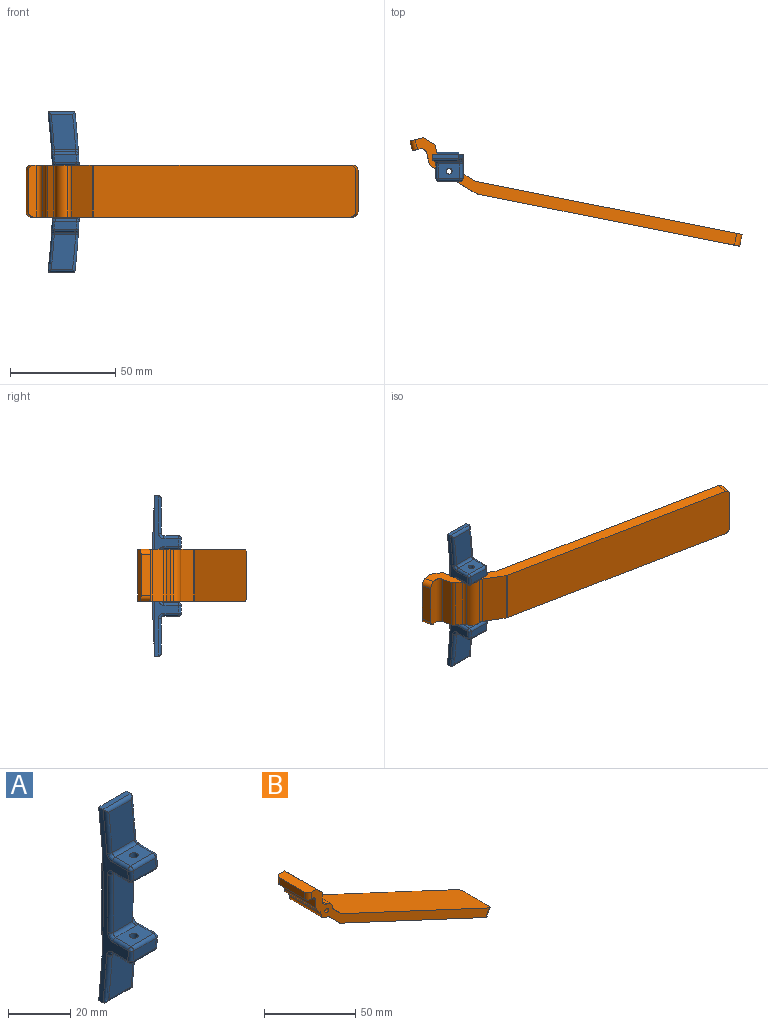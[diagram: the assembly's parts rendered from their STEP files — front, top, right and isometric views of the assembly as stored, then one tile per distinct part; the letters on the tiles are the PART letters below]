
ASSEMBLY  parts=2 mates=1
PART A: 67 faces, bbox 38x38x76.8 mm
  f0: plane 76.2x2.54mm, normal (0,1,0), area 76.9mm2, adj f4,f8,f13,f65
  f1: plane 10.16x6.99mm, normal (0,0,-1), area 64.9mm2, adj f16,f28,f29,f37,f38
  f2: cylinder r=317.5mm len=76.2mm, axis (0,1,0), area 184.2mm2, adj f6,f8,f13,f26,f27,f31,f32,f36
  f3: plane 10.16x7.63mm, normal (0,0,1), area 65.1mm2, adj f16,f45,f51,f56,f59,f60
  f4: cylinder r=317.5mm len=76.2mm, axis (0,1,0), area 230.8mm2, adj f0,f8,f13,f18,f19,f20,f23,f24
  f5: plane 10.35x3.81mm, normal (0,-1,0), area 38.7mm2, adj f38,f39,f50,f51
  f6: plane 76.2x2.29mm, normal (0,1,0), area 116.6mm2, adj f2,f66
  f7: plane 16.51x11.64mm, normal (0,-1,0), area 167.6mm2, adj f18,f21,f25,f26
  f8: plane 12.7x1.91mm, normal (0,0,1), area 24.2mm2, adj f0,f2,f4,f21,f64
  f9: plane 10.35x3.81mm, normal (0,-1,0), area 38.7mm2, adj f34,f35,f48,f49
  f10: plane 10.16x6.99mm, normal (0,0,1), area 64.9mm2, adj f15,f24,f25,f35,f36
  f11: plane 10.16x7.63mm, normal (0,0,-1), area 65.1mm2, adj f15,f40,f48,f53,f57,f58
  f12: plane 22.86x9.1mm, normal (0,-1,0), area 203.2mm2, adj f17,f46,f53,f56,f57,f60
  f13: plane 12.7x1.91mm, normal (0,0,-1), area 24.2mm2, adj f0,f2,f4,f22,f64
  f14: plane 16.51x11.64mm, normal (0,-1,0), area 167.6mm2, adj f19,f22,f27,f28
  f15: cylinder r=1.39mm len=6.35mm, axis (0,0,1), area 55.4mm2, adj f10,f11
  f16: cylinder r=1.39mm len=6.35mm, axis (0,0,1), area 55.4mm2, adj f1,f3
  f17: cone r=314.96mm half-angle=45deg, axis (0,1,0), area 69.9mm2, adj f12,f57,f60,f63
  f18: torus R=318.77mm, axis (0,-1,0), area 34.4mm2, adj f4,f7,f20,f21
  f19: torus R=318.77mm, axis (0,-1,0), area 34.4mm2, adj f4,f14,f22,f23
  f20: bspline ~3.11x2.96mm, area 5.5mm2, adj f4,f18,f24,f25
  f21: cylinder r=1.27mm len=12.7mm, axis (1,0,0), area 22.8mm2, adj f7,f8,f18,f26
  f22: cylinder r=1.27mm len=12.7mm, axis (-1,0,0), area 22.8mm2, adj f13,f14,f19,f27
  f23: bspline ~3.1x2.98mm, area 5.5mm2, adj f4,f19,f28,f29
  f24: cylinder r=1.27mm len=6.99mm, axis (0,1,0), area 14.4mm2, adj f4,f10,f20,f30
  f25: cylinder r=1.27mm len=10.31mm, axis (-1,0,0), area 20.3mm2, adj f7,f10,f20,f31
  f26: torus R=316.23mm, axis (0,-1,0), area 34.3mm2, adj f2,f7,f21,f31
  f27: torus R=316.23mm, axis (0,-1,0), area 34.3mm2, adj f2,f14,f22,f32
  f28: cylinder r=1.27mm len=10.31mm, axis (1,0,0), area 20.3mm2, adj f1,f14,f23,f32
  f29: cylinder r=1.27mm len=6.99mm, axis (0,1,0), area 14.4mm2, adj f1,f4,f23,f33
  f30: sphere r=1.27mm, area 1.7mm2, adj f24,f34,f35
  f31: bspline ~3.12x2.98mm, area 5.3mm2, adj f2,f25,f26,f36
  f32: bspline ~3.11x2.99mm, area 5.3mm2, adj f2,f27,f28,f37
  f33: sphere r=1.27mm, area 2.6mm2, adj f29,f38,f39
  f34: torus R=318.77mm, axis (0,-1,0), area 7.6mm2, adj f4,f9,f30,f41
  f35: cylinder r=1.27mm len=10.16mm, axis (1,0,0), area 20.3mm2, adj f9,f10,f30,f42
  f36: cylinder r=1.27mm len=6.99mm, axis (0,1,0), area 13.4mm2, adj f2,f10,f31,f42
  f37: cylinder r=1.27mm len=6.99mm, axis (0,1,0), area 13.4mm2, adj f1,f2,f32,f43
  f38: cylinder r=1.27mm len=10.16mm, axis (-1,0,0), area 20.3mm2, adj f1,f5,f33,f43
  f39: torus R=318.77mm, axis (0,-1,0), area 7.6mm2, adj f4,f5,f33,f44
  f40: cylinder r=1.27mm len=6.99mm, axis (0,1,0), area 13.5mm2, adj f4,f11,f41,f47
  f41: sphere r=1.27mm, area 2.5mm2, adj f34,f40,f48
  f42: sphere r=1.27mm, area 2.4mm2, adj f35,f36,f49
  f43: sphere r=1.27mm, area 3.4mm2, adj f37,f38,f50
  f44: sphere r=1.27mm, area 1.6mm2, adj f39,f45,f51
  f45: cylinder r=1.27mm len=6.99mm, axis (0,1,0), area 13.5mm2, adj f3,f4,f44,f52
  f46: torus R=318.77mm, axis (0,-1,0), area 45.5mm2, adj f4,f12,f47,f52
  f47: bspline ~3.1x2.98mm, area 5.4mm2, adj f4,f40,f46,f53
  f48: cylinder r=1.27mm len=10.16mm, axis (-1,0,0), area 20.3mm2, adj f9,f11,f41,f54
  f49: torus R=316.23mm, axis (0,-1,0), area 7.6mm2, adj f2,f9,f42,f54
  f50: torus R=316.23mm, axis (0,-1,0), area 7.6mm2, adj f2,f5,f43,f55
  f51: cylinder r=1.27mm len=10.16mm, axis (1,0,0), area 20.3mm2, adj f3,f5,f44,f55
  f52: bspline ~3.11x2.96mm, area 5.4mm2, adj f4,f45,f46,f56
  f53: cylinder r=1.27mm len=9.52mm, axis (1,0,0), area 18.4mm2, adj f11,f12,f47,f57
  f54: sphere r=1.27mm, area 3.5mm2, adj f48,f49,f58
  f55: sphere r=1.27mm, area 2.6mm2, adj f50,f51,f59
  f56: cylinder r=1.27mm len=9.52mm, axis (-1,0,0), area 18.4mm2, adj f3,f12,f52,f60
  f57: bspline ~38.03x38.01mm, area 4.6mm2, adj f11,f12,f17,f53,f61
  f58: cylinder r=1.27mm len=7.63mm, axis (0,1,0), area 15.6mm2, adj f2,f11,f54,f61
  f59: cylinder r=1.27mm len=7.63mm, axis (0,1,0), area 15.6mm2, adj f2,f3,f55,f62
  f60: bspline ~38.03x38.01mm, area 4.6mm2, adj f3,f12,f17,f56,f62
  f61: bspline ~3.93x2.92mm, area 5.9mm2, adj f2,f57,f58,f63
  f62: bspline ~3.86x3.06mm, area 5.9mm2, adj f2,f59,f60,f63
  f63: torus R=316.23mm, axis (0,-1,0), area 22.8mm2, adj f2,f17,f61,f62
  f64: cylinder r=572.13mm len=76.2mm, axis (1,0,0), area 774.8mm2, adj f8,f13,f65,f66
  f65: plane 76.2x1.27mm, normal (-1,0,0), area 64.5mm2, adj f0,f64
  f66: plane 76.2x1.27mm, normal (1,0,0), area 64.5mm2, adj f6,f64
PART B: 31 faces, bbox 142.9x24.6x85.9 mm
  f0: plane 24.64x5.48mm, normal (0.71,0,0.71), area 190.8mm2, adj f7,f19,f20,f25
  f1: plane 24.64x8.12mm, normal (-0.71,0,-0.71), area 282.9mm2, adj f3,f19,f20,f23
  f2: plane 24.64x2.38mm, normal (-0.71,0,-0.71), area 82.9mm2, adj f18,f19,f20,f24
  f3: cylinder r=2.54mm len=24.64mm, axis (0,1,0), area 21.8mm2, adj f1,f4,f19,f20
  f4: plane 115.1x53.67mm, normal (-0.42,0,-0.91), area 3126.3mm2, adj f3,f5,f19,f20,f28,f30
  f5: plane 19.56x5.22mm, normal (0.91,0,-0.42), area 112.5mm2, adj f4,f6,f28,f30
  f6: plane 116.81x54.47mm, normal (0.42,0,0.91), area 3172.7mm2, adj f5,f7,f19,f20,f28,f30
  f7: cylinder r=2.54mm len=24.64mm, axis (0,1,0), area 21.8mm2, adj f0,f6,f19,f20
  f8: plane 24.64x0.99mm, normal (0.71,0,0.71), area 34.3mm2, adj f9,f19,f20,f26
  f9: cylinder r=2.54mm len=24.64mm, axis (0,1,0), area 49.2mm2, adj f8,f10,f19,f20
  f10: plane 24.64x5.93mm, normal (1,0,0), area 146.2mm2, adj f9,f11,f19,f20
  f11: plane 24.64x4.49mm, normal (0.71,0,0.71), area 156.5mm2, adj f10,f12,f19,f20
  f12: plane 24.64x6.62mm, normal (0,0,1), area 160.4mm2, adj f11,f13,f19,f20,f27,f29
  f13: plane 19.56x4.78mm, normal (-1,0,0), area 93.4mm2, adj f12,f14,f27,f29
  f14: plane 24.64x3.81mm, normal (0,0,-1), area 91.1mm2, adj f13,f15,f19,f20,f27,f29
  f15: cylinder r=2.54mm len=24.64mm, axis (0,1,0), area 98.3mm2, adj f14,f16,f19,f20
  f16: plane 24.64x5.08mm, normal (-1,0,0), area 125.2mm2, adj f15,f18,f19,f20
  f17: cylinder r=1.38mm len=24.64mm, axis (0,1,0), area 214.3mm2, adj f19,f20
  f18: cylinder r=2.54mm len=24.64mm, axis (0,1,0), area 49.2mm2, adj f2,f16,f19,f20
  f19: plane 138.02x84.81mm, normal (0,-1,0), area 921.1mm2, adj f0,f1,f2,f3,f4,f6,f7,f8
  f20: plane 138.02x84.81mm, normal (0,1,0), area 921.1mm2, adj f0,f1,f2,f3,f4,f6,f7,f8
  f21: cylinder r=4.45mm len=24.64mm, axis (0,-1,0), area 172.8mm2, adj f19,f20,f23,f24
  f22: cylinder r=4.45mm len=24.64mm, axis (0,-1,0), area 172.8mm2, adj f19,f20,f25,f26
  f23: cylinder r=2.54mm len=24.64mm, axis (0,-1,0), area 49.4mm2, adj f1,f19,f20,f21
  f24: cylinder r=2.54mm len=24.64mm, axis (0,-1,0), area 49.4mm2, adj f2,f19,f20,f21
  f25: cylinder r=2.54mm len=24.64mm, axis (0,-1,0), area 49.4mm2, adj f0,f19,f20,f22
  f26: cylinder r=2.54mm len=24.64mm, axis (0,-1,0), area 49.4mm2, adj f8,f19,f20,f22
  f27: cylinder r=2.54mm len=4.78mm, axis (0,0,-1), area 19.1mm2, adj f12,f13,f14,f20
  f28: cylinder r=2.54mm len=6.29mm, axis (0.42,0,0.91), area 23mm2, adj f4,f5,f6,f20
  f29: cylinder r=2.54mm len=4.78mm, axis (0,0,1), area 19.1mm2, adj f12,f13,f14,f19
  f30: cylinder r=2.54mm len=6.29mm, axis (-0.42,0,-0.91), area 23mm2, adj f4,f5,f6,f19
PLACE A t=(6.35,0.95,38.1)mm
PLACE B rot(axis=(-0.99,-0.12,0.12),90.8deg) t=(15.36,-17.87,26.16)mm
MATE revolute B.f17 <-> A.f15  axis (0,0,1) through (1.72,-6.98,50.8)mm
